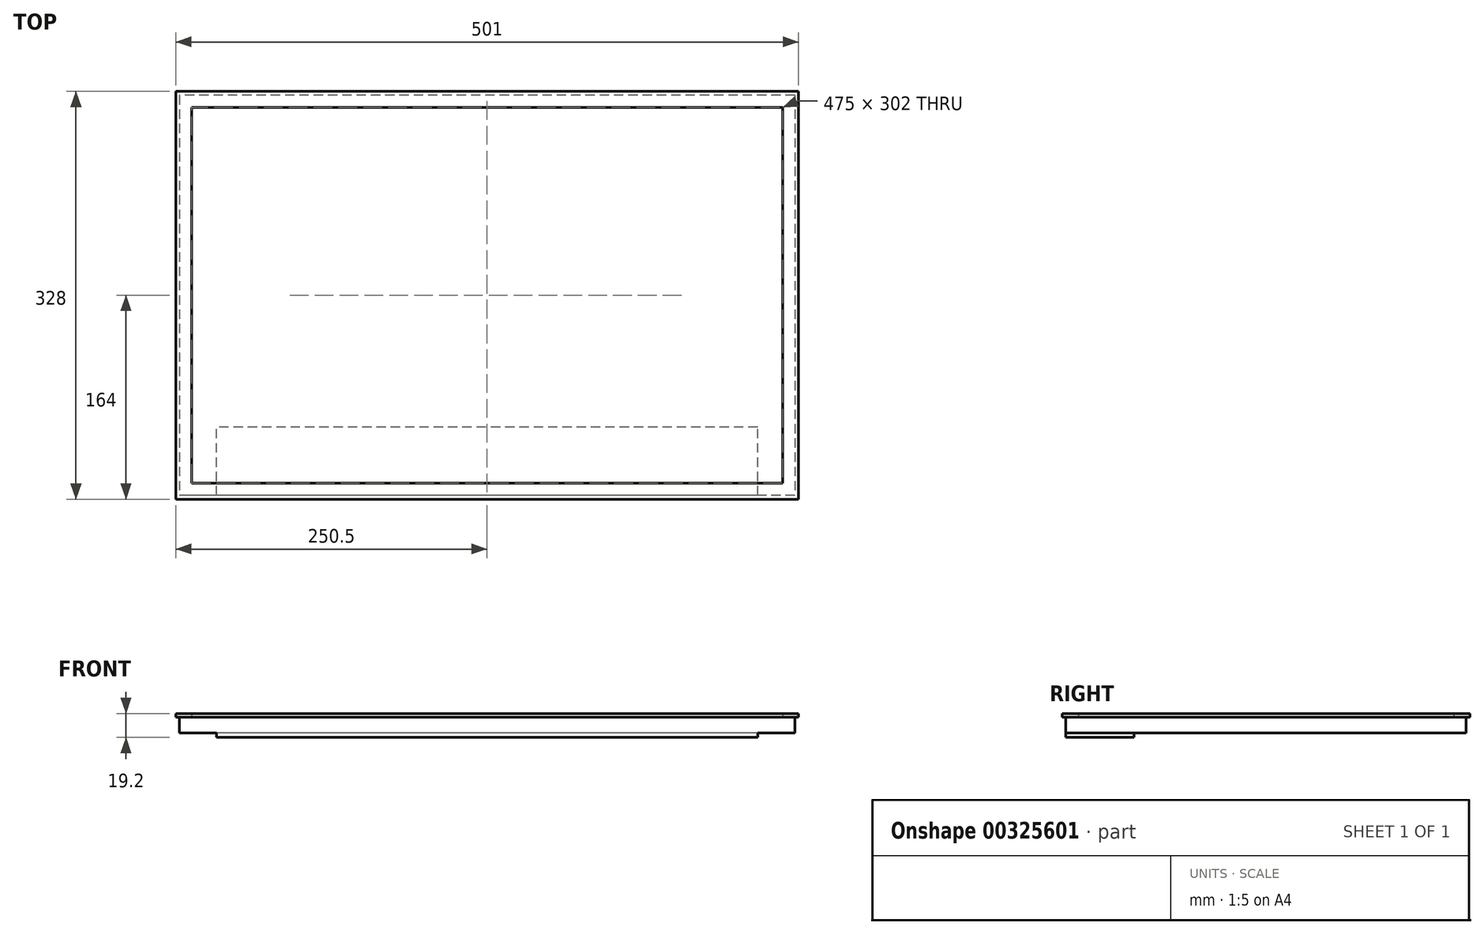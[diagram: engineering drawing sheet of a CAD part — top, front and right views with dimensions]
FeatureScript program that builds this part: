
annotation { "Feature Type Name" : "Feature", "Feature Type Description" : "" }
export const myFeature = defineFeature(function(context is Context, id is Id, definition is map)
    precondition{}
    {
        {
            var Q0;
            Q0=qCreatedBy(makeId("Top.planeOp"),FACE);
            var sketch = newSketch(context, id + "F0", { "sketchPlane" : qUnion([Q0])});
            skLineSegment(sketch, "E0.bottom", {"start": v(247.5, 161) * mm, "end": v(-247.5, 161) * mm});
            skLineSegment(sketch, "E0.top", {"start": v(247.5, -161) * mm, "end": v(-247.5, -161) * mm});
            skLineSegment(sketch, "E0.left", {"start": v(247.5, 161) * mm, "end": v(247.5, -161) * mm});
            skLineSegment(sketch, "E0.right", {"start": v(-247.5, 161) * mm, "end": v(-247.5, -161) * mm});
            skPoint(sketch, "E0.middle", {"position": v(0, 0) * mm});
            skSolve(sketch);
        }
        {
            var Q0;
            Q0=makeQuery(id+"F0.imprint","IMPRINT",FACE,{"disambiguationData":[TD([[makeQuery(id+"F0.imprint","IMPRINT",EDGE,{"derivedFrom":sQuery(id+"F0.wireOp",EDGE,"E0.bottom")}),1.0]])]});
            extrude(context, id + "F1", {"entities" : qUnion([Q0]), "depth" : 12.7 * mm});
        }
        {
            var Q0;
            Q0=makeQuery(id+"F1.opExtrude","CAP_FACE",FACE,{"disambiguationData":[OSD([sQuery(id+"F0.wireOp",EDGE,"E0.bottom"),sQuery(id+"F0.wireOp",EDGE,"E0.top"),sQuery(id+"F0.wireOp",EDGE,"E0.left"),sQuery(id+"F0.wireOp",EDGE,"E0.right")])],"isStart":true});
            var sketch = newSketch(context, id + "F2", { "sketchPlane" : qUnion([Q0])});
            skLineSegment(sketch, "E1.bottom", {"start": v(217.5, 161) * mm, "end": v(-217.5, 161) * mm});
            skLineSegment(sketch, "E1.top", {"start": v(217.5, 106) * mm, "end": v(-217.5, 106) * mm});
            skLineSegment(sketch, "E1.left", {"start": v(217.5, 161) * mm, "end": v(217.5, 106) * mm});
            skLineSegment(sketch, "E1.right", {"start": v(-217.5, 161) * mm, "end": v(-217.5, 106) * mm});
            skSolve(sketch);
        }
        {
            var Q0;
            Q0=makeQuery(id+"F2.imprint","IMPRINT",FACE,{"disambiguationData":[TD([[makeQuery(id+"F2.imprint","IMPRINT",EDGE,{"derivedFrom":sQuery(id+"F2.wireOp",EDGE,"E1.bottom")}),1.0]])]});
            extrude(context, id + "F3", {"entities" : qUnion([Q0]), "operationType" : NewBodyOperationType.ADD, "depth" : 3.5 * mm});
        }
        {
            var Q0;
            Q0=makeQuery(id+"F1.opExtrude","CAP_FACE",FACE,{"disambiguationData":[OSD([sQuery(id+"F0.wireOp",EDGE,"E0.bottom"),sQuery(id+"F0.wireOp",EDGE,"E0.top"),sQuery(id+"F0.wireOp",EDGE,"E0.left"),sQuery(id+"F0.wireOp",EDGE,"E0.right")])],"isStart":false});
            var sketch = newSketch(context, id + "F4", { "sketchPlane" : qUnion([Q0])});
            skLineSegment(sketch, "E2.bottom", {"start": v(237.5, 151) * mm, "end": v(-237.5, 151) * mm});
            skLineSegment(sketch, "E2.top", {"start": v(237.5, -151) * mm, "end": v(-237.5, -151) * mm});
            skLineSegment(sketch, "E2.left", {"start": v(237.5, 151) * mm, "end": v(237.5, -151) * mm});
            skLineSegment(sketch, "E2.right", {"start": v(-237.5, 151) * mm, "end": v(-237.5, -151) * mm});
            skPoint(sketch, "E2.middle", {"position": v(0, 0) * mm});
            skLineSegment(sketch, "E3.bottom", {"start": v(-250.5, 164) * mm, "end": v(250.5, 164) * mm});
            skLineSegment(sketch, "E3.top", {"start": v(-250.5, -164) * mm, "end": v(250.5, -164) * mm});
            skLineSegment(sketch, "E3.left", {"start": v(-250.5, 164) * mm, "end": v(-250.5, -164) * mm});
            skLineSegment(sketch, "E3.right", {"start": v(250.5, 164) * mm, "end": v(250.5, -164) * mm});
            skSolve(sketch);
        }
        {
            var Q0;
            Q0 = qSketchRegion(id + "F4", true);
            extrude(context, id + "F5", {"entities" : qUnion([Q0]), "depth" : 3 * mm});
        }
    });
